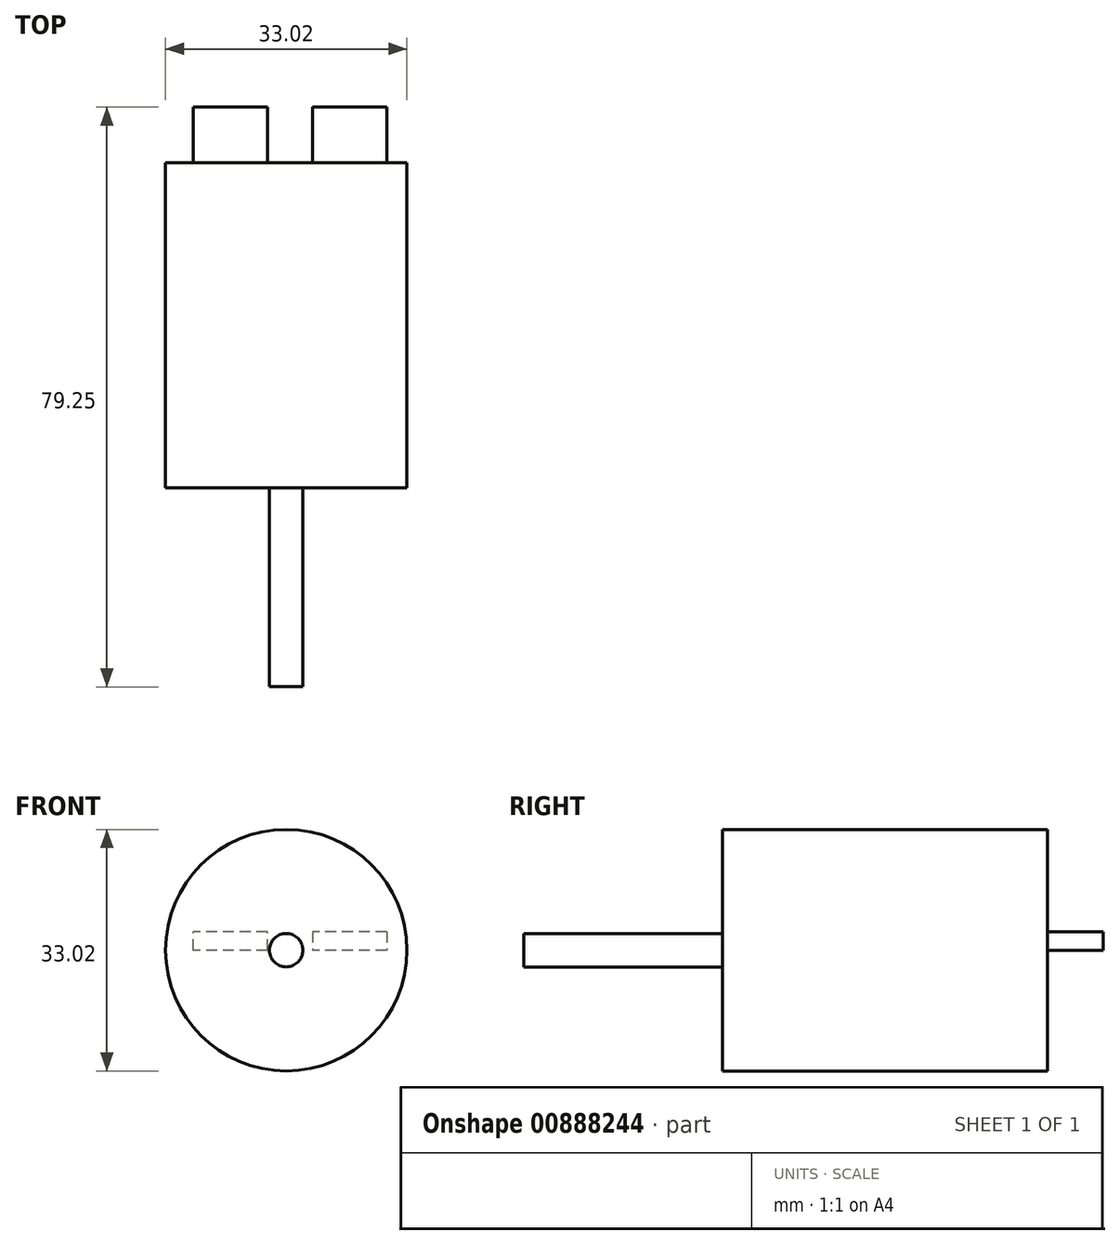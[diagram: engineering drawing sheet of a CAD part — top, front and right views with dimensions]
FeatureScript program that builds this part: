
annotation { "Feature Type Name" : "Feature", "Feature Type Description" : "" }
export const myFeature = defineFeature(function(context is Context, id is Id, definition is map)
    precondition{}
    {
        {
            var Q0;
            Q0=qCreatedBy(makeId("Front.planeOp"),FACE);
            var sketch = newSketch(context, id + "F0", { "sketchPlane" : qUnion([Q0])});
            skCircle(sketch, "E0", {"center": v(0, 0) * mm, "radius": 16.51 * mm});
            skSolve(sketch);
        }
        {
            var Q0;
            Q0=qSketchRegion(id+"F0",true);
            extrude(context, id + "F1", {"entities" : qUnion([Q0]), "depth" : 44.45 * mm, "offsetDistance" : 25.4 * mm});
        }
        {
            var Q0;
            Q0=makeQuery(id+"F1.opExtrude","CAP_FACE",FACE,{"disambiguationData":[OSD([sQuery(id+"F0.wireOp",EDGE,"E0")])],"isStart":false});
            var sketch = newSketch(context, id + "F2", { "sketchPlane" : qUnion([Q0])});
            skCircle(sketch, "E1", {"center": v(0, 0) * mm, "radius": 2.29 * mm});
            skSolve(sketch);
        }
        {
            var Q0;
            Q0=makeQuery(id+"F2.imprint","IMPRINT",FACE,{"disambiguationData":[TD([[makeQuery(id+"F2.imprint","IMPRINT",EDGE,{"derivedFrom":sQuery(id+"F2.wireOp",EDGE,"E1")}),1.0]])]});
            extrude(context, id + "F3", {"entities" : qUnion([Q0]), "operationType" : NewBodyOperationType.ADD, "depth" : 27.18 * mm, "offsetDistance" : 25.4 * mm});
        }
        {
            var Q0;
            Q0=makeQuery(id+"F1.opExtrude","CAP_FACE",FACE,{"disambiguationData":[OSD([sQuery(id+"F0.wireOp",EDGE,"E0")])],"isStart":true});
            var sketch = newSketch(context, id + "F4", { "sketchPlane" : qUnion([Q0])});
            skLineSegment(sketch, "E2.bottom", {"start": v(-13.74, 2.54) * mm, "end": v(-3.58, 2.54) * mm});
            skLineSegment(sketch, "E2.top", {"start": v(-13.74, 0) * mm, "end": v(-3.58, 0) * mm});
            skLineSegment(sketch, "E2.left", {"start": v(-13.74, 2.54) * mm, "end": v(-13.74, 0) * mm});
            skLineSegment(sketch, "E2.right", {"start": v(-3.58, 2.54) * mm, "end": v(-3.58, 0) * mm});
            skLineSegment(sketch, "E3.bottom", {"start": v(2.57, 0) * mm, "end": v(12.73, 0) * mm});
            skLineSegment(sketch, "E3.top", {"start": v(2.57, 2.54) * mm, "end": v(12.73, 2.54) * mm});
            skLineSegment(sketch, "E3.left", {"start": v(2.57, 0) * mm, "end": v(2.57, 2.54) * mm});
            skLineSegment(sketch, "E3.right", {"start": v(12.73, 0) * mm, "end": v(12.73, 2.54) * mm});
            skSolve(sketch);
        }
        {
            var Q0;
            Q0=qSketchRegion(id+"F4",true);
            extrude(context, id + "F5", {"entities" : qUnion([Q0]), "operationType" : NewBodyOperationType.ADD, "depth" : 7.62 * mm, "offsetDistance" : 25.4 * mm});
        }
    });
